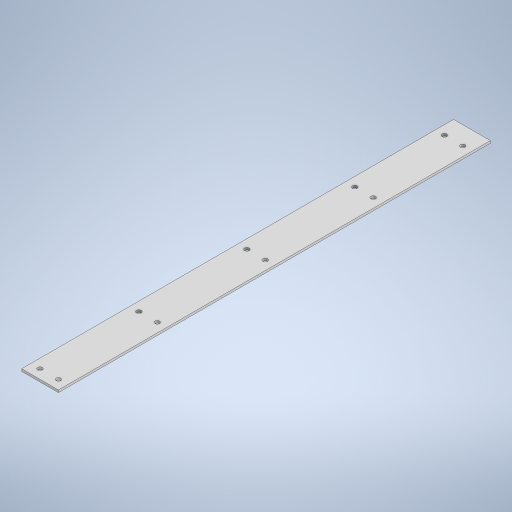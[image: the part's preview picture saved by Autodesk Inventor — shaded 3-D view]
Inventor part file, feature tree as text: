
AUTODESK INVENTOR PART (.ipt)
format: ipt  version: 2023 (Build 270158030, 158C)  size: 258,560 bytes
history: native  units: in
note: dims shown in document units (in); Inventor stores cm internally (conversion verified against a paired STEP export)
features: extrude x1, sketch x1
ambient origin geometry x8: Origin, YZ Plane, XZ Plane, XY Plane, X Axis, Y Axis, Z Axis, Center Point
bodies: Solid1 (feature_tree)
feature tree (2):
  extrude  "Extrusion1"  Depth=23.5in
  sketch  "Sketch1"  dims[d0=2.0in d1=23.5in d2=0.125in d3=0.0in d4=0.25in d5=0.5in d6=0.5in d11=0.25in d12=11.75in d13=0.25in d14=5.875in]
